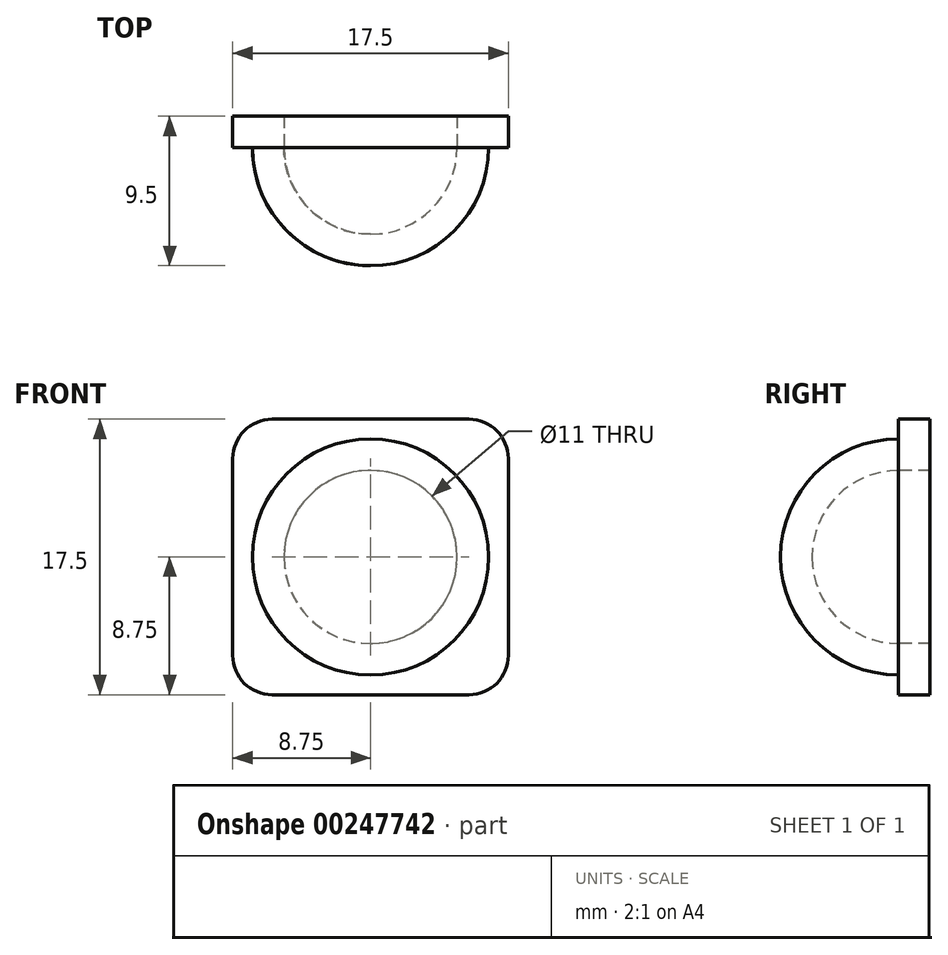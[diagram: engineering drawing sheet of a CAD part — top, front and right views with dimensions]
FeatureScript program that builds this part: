
annotation { "Feature Type Name" : "Feature", "Feature Type Description" : "" }
export const myFeature = defineFeature(function(context is Context, id is Id, definition is map)
    precondition{}
    {
        {
            var Q0;
            Q0=qCreatedBy(makeId("Top.planeOp"),FACE);
            var sketch = newSketch(context, id + "F0", { "sketchPlane" : qUnion([Q0])});
            skCircle(sketch, "E0", {"center": v(0, 0) * mm, "radius": 7.5 * mm});
            skLineSegment(sketch, "E1", {"start": v(-7.5, 0) * mm, "end": v(7.5, 0) * mm});
            skLineSegment(sketch, "E2", {"start": v(0, 0) * mm, "end": v(0, -7.5) * mm});
            skSolve(sketch);
        }
        {
            var Q0;
            {var subQ3=sQuery(id+"F0.wireOp",EDGE,"E2");Q0=makeQuery(id+"F0.imprint","IMPRINT",FACE,{"disambiguationData":[TD([[makeQuery(id+"F0.imprint","IMPRINT",EDGE,{"derivedFrom":subQ3}),-1.0]])]});}
            var Q1;
            Q1=sQuery(id+"F0.wireOp",EDGE,"E2");
            revolve(context, id + "F1", {"entities" : qUnion([Q0]), "axis" : qUnion([Q1]), "revolveType" : RevolveType.FULL});
        }
        {
            var Q0;
            Q0=makeQuery(id+"F1.opRevolve","SWEPT_FACE",FACE,{"disambiguationData":[OSD([sQuery(id+"F0.wireOp",EDGE,"E1")])]});
            shell(context, id + "F2", {"entities" : qUnion([Q0]), "thickness" : 2 * mm});
        }
        {
            var Q0;
            Q0=makeQuery(id+"F1.opRevolve","SWEPT_FACE",FACE,{"disambiguationData":[OSD([sQuery(id+"F0.wireOp",EDGE,"E1")])]});
            var sketch = newSketch(context, id + "F3", { "sketchPlane" : qUnion([Q0])});
            skCircle(sketch, "E3.0.0", {"center": v(0, 0) * mm, "radius": 7.5 * mm});
            skCircle(sketch, "E4.0", {"center": v(0, 0) * mm, "radius": 5.5 * mm});
            skLineSegment(sketch, "E5.bottom", {"start": v(6.25, -8.75) * mm, "end": v(-6.25, -8.75) * mm});
            skLineSegment(sketch, "E5.top", {"start": v(6.25, 8.75) * mm, "end": v(-6.25, 8.75) * mm});
            skLineSegment(sketch, "E5.left", {"start": v(8.75, -6.25) * mm, "end": v(8.75, 6.25) * mm});
            skLineSegment(sketch, "E5.right", {"start": v(-8.75, -6.25) * mm, "end": v(-8.75, 6.25) * mm});
            skPoint(sketch, "E6.visualSharp", {"position": v(-8.75, 8.75) * mm});
            skArc(sketch, "E6.filletArc", {"start": v(-6.25, 8.75) * mm, "mid": v(-8.02, 8.02) * mm, "end": v(-8.75, 6.25) * mm});
            skPoint(sketch, "E7.visualSharp", {"position": v(8.75, 8.75) * mm});
            skArc(sketch, "E7.filletArc", {"start": v(8.75, 6.25) * mm, "mid": v(8.02, 8.02) * mm, "end": v(6.25, 8.75) * mm});
            skPoint(sketch, "E8.visualSharp", {"position": v(-8.75, -8.75) * mm});
            skArc(sketch, "E8.filletArc", {"start": v(-8.75, -6.25) * mm, "mid": v(-8.02, -8.02) * mm, "end": v(-6.25, -8.75) * mm});
            skPoint(sketch, "E9.visualSharp", {"position": v(8.75, -8.75) * mm});
            skArc(sketch, "E9.filletArc", {"start": v(6.25, -8.75) * mm, "mid": v(8.02, -8.02) * mm, "end": v(8.75, -6.25) * mm});
            skSolve(sketch);
        }
        {
            var Q0;
            Q0 = qSketchRegion(id + "F3", true);
            var Q1;
            Q1=makeQuery(id+"F3.imprint","IMPRINT",FACE,{"disambiguationData":[TD([[makeQuery(id+"F3.imprint","IMPRINT",EDGE,{"derivedFrom":sQuery(id+"F3.wireOp",EDGE,"E3.0.0")}),1.0]])]});
            extrude(context, id + "F4", {"entities" : qUnion([Q0, Q1]), "operationType" : NewBodyOperationType.ADD, "depth" : 2 * mm});
        }
    });
